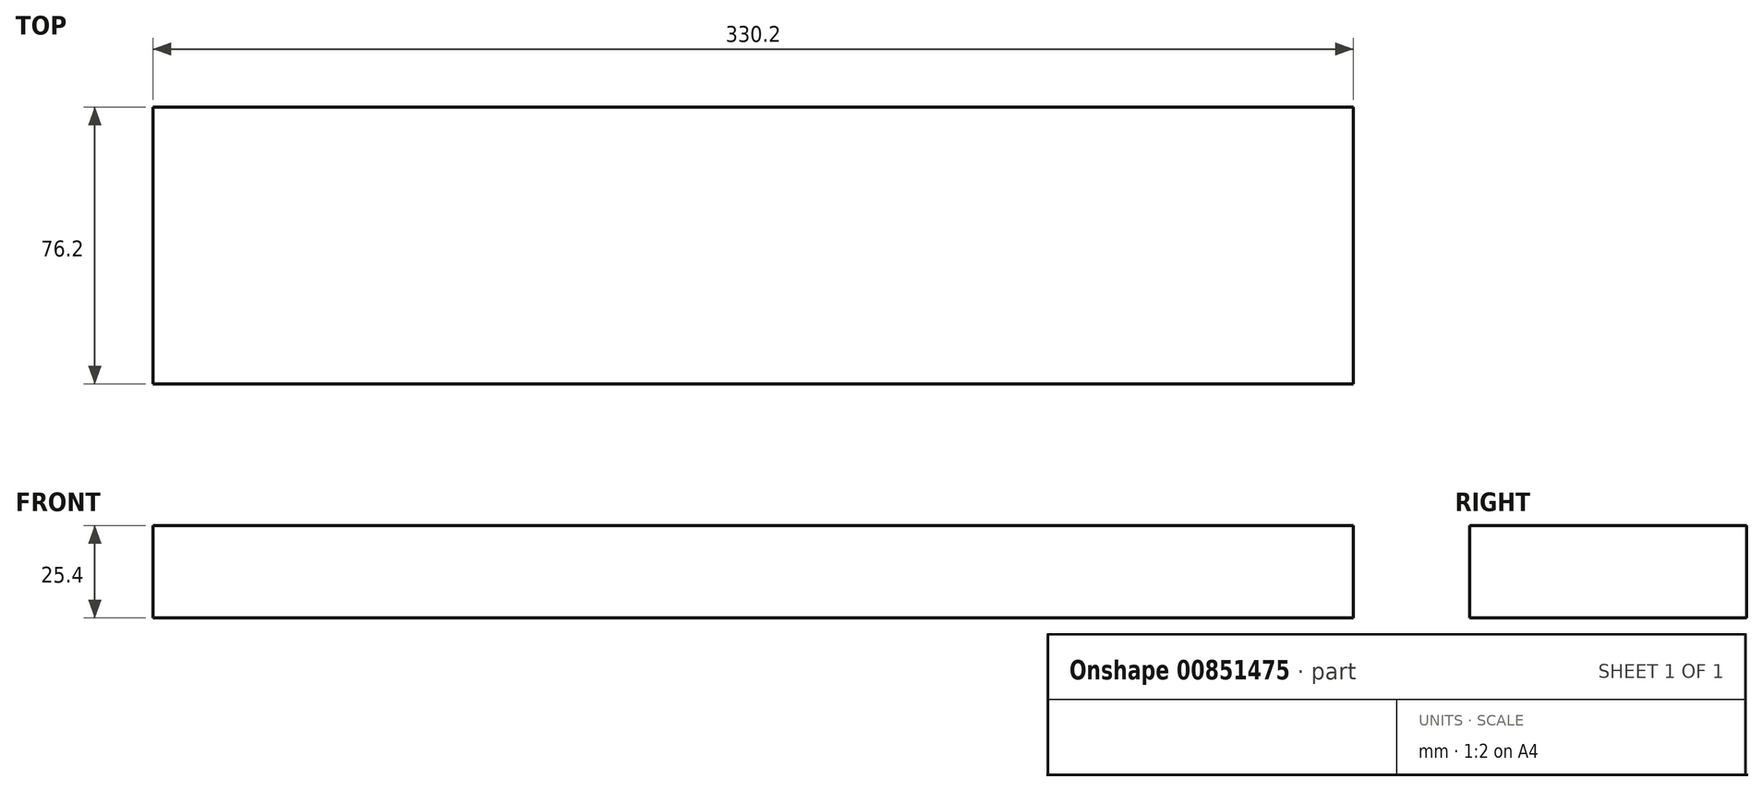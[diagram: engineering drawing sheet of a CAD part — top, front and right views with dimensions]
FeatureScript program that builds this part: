
annotation { "Feature Type Name" : "Feature", "Feature Type Description" : "" }
export const myFeature = defineFeature(function(context is Context, id is Id, definition is map)
    precondition{}
    {
        {
            var Q0;
            Q0=qCreatedBy(makeId("Front.planeOp"),FACE);
            var sketch = newSketch(context, id + "F0", { "sketchPlane" : qUnion([Q0])});
            skLineSegment(sketch, "E0.bottom", {"start": v(-14.43, 40.94) * mm, "end": v(315.77, 40.94) * mm});
            skLineSegment(sketch, "E0.top", {"start": v(-14.43, 15.54) * mm, "end": v(315.77, 15.54) * mm});
            skLineSegment(sketch, "E0.left", {"start": v(-14.43, 40.94) * mm, "end": v(-14.43, 15.54) * mm});
            skLineSegment(sketch, "E0.right", {"start": v(315.77, 40.94) * mm, "end": v(315.77, 15.54) * mm});
            skSolve(sketch);
        }
        {
            var Q0;
            Q0 = qSketchRegion(id + "F0", true);
            extrude(context, id + "F1", {"entities" : qUnion([Q0]), "depth" : 76.2 * mm, "offsetDistance" : 25 * mm});
        }
    });
